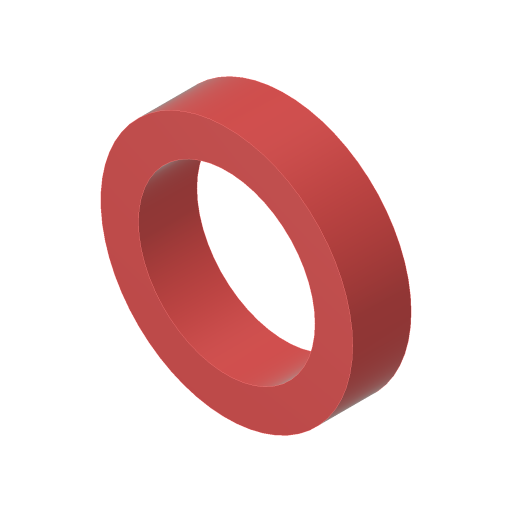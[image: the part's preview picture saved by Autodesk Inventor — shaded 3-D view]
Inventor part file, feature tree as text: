
AUTODESK INVENTOR PART (.ipt)
format: ipt  version: 2023.4 (Build 274418000, 418)  size: 112,128 bytes
history: native  units: in
note: dims shown in document units (in); Inventor stores cm internally (conversion verified against a paired STEP export)
features: extrude x1, sketch x1
ambient origin geometry x8: Origin, YZ Plane, XZ Plane, XY Plane, X Axis, Y Axis, Z Axis, Center Point
bodies: Solid1 (feature_tree)
feature tree (2):
  extrude  "Extrusion1"  Depth=0.194in
  sketch  "Sketch1"  dims[d0=0.585in d1=0.125in d2=0.194in d3=0.0in]
